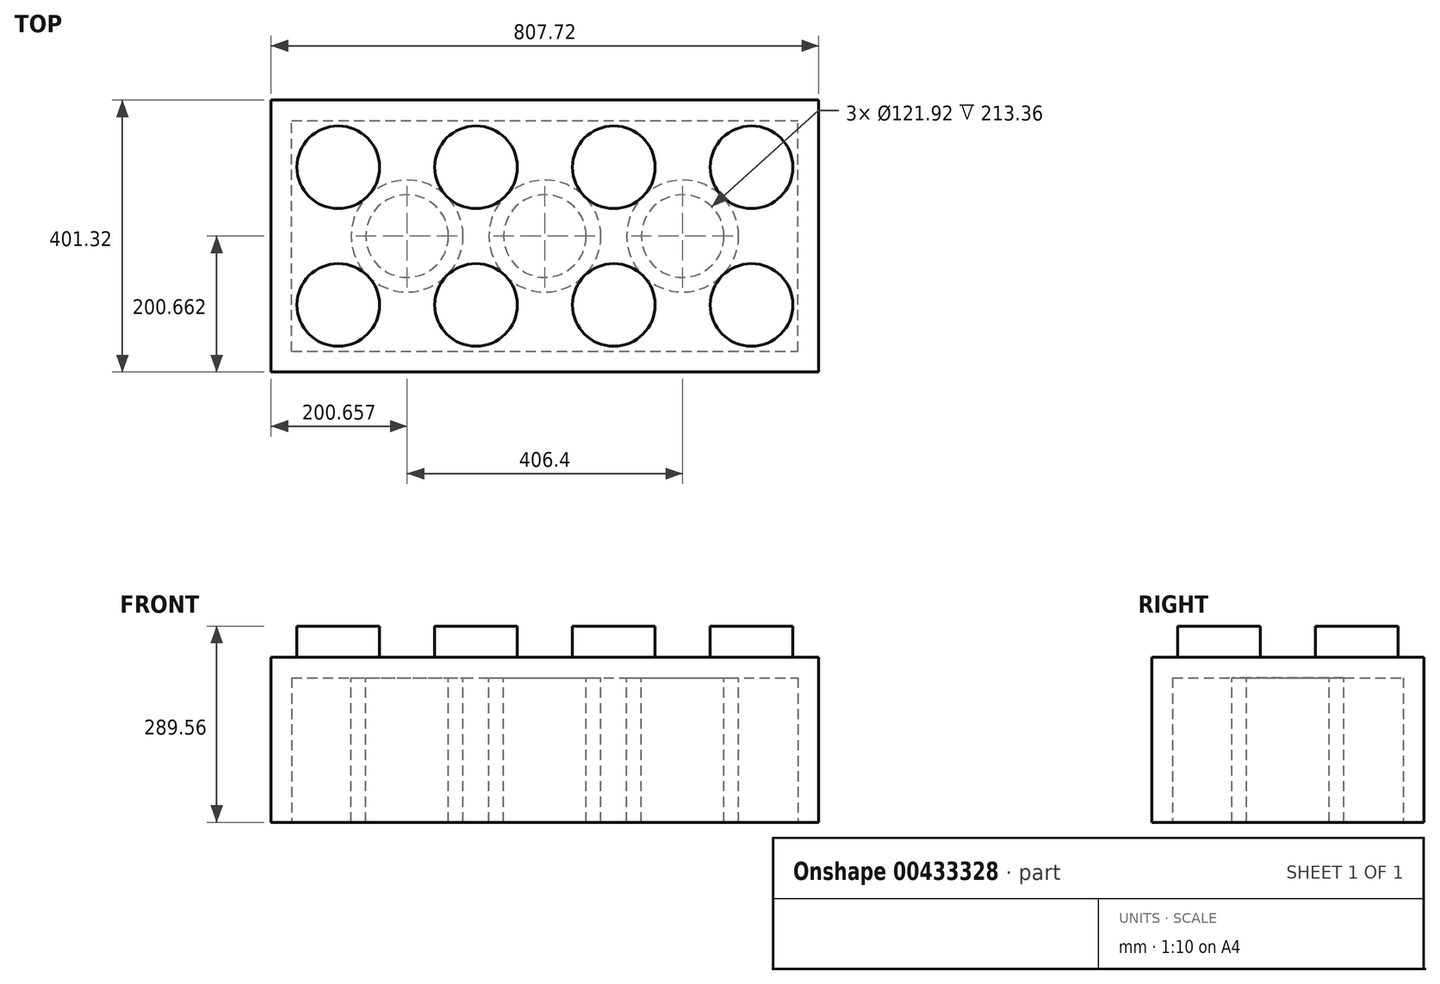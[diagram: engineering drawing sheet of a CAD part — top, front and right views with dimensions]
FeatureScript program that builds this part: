
annotation { "Feature Type Name" : "Feature", "Feature Type Description" : "" }
export const myFeature = defineFeature(function(context is Context, id is Id, definition is map)
    precondition{}
    {
        {
            var Q0;
            Q0=qCreatedBy(makeId("Top.planeOp"),FACE);
            var sketch = newSketch(context, id + "F0", { "sketchPlane" : qUnion([Q0])});
            skLineSegment(sketch, "E0.bottom", {"start": v(-348.7, 195.86) * mm, "end": v(459.02, 195.86) * mm});
            skLineSegment(sketch, "E0.top", {"start": v(-348.7, -205.46) * mm, "end": v(459.02, -205.46) * mm});
            skLineSegment(sketch, "E0.left", {"start": v(-348.7, 195.86) * mm, "end": v(-348.7, -205.46) * mm});
            skLineSegment(sketch, "E0.right", {"start": v(459.02, 195.86) * mm, "end": v(459.02, -205.46) * mm});
            skSolve(sketch);
        }
        {
            var Q0;
            Q0 = qSketchRegion(id + "F0", true);
            extrude(context, id + "F1", {"entities" : qUnion([Q0]), "depth" : 243.84 * mm});
        }
        {
            var Q0;
            Q0=makeQuery(id+"F1.opExtrude","CAP_FACE",FACE,{"disambiguationData":[OSD([sQuery(id+"F0.wireOp",EDGE,"E0.bottom"),sQuery(id+"F0.wireOp",EDGE,"E0.top"),sQuery(id+"F0.wireOp",EDGE,"E0.left"),sQuery(id+"F0.wireOp",EDGE,"E0.right")])],"isStart":false});
            var sketch = newSketch(context, id + "F2", { "sketchPlane" : qUnion([Q0])});
            skCircle(sketch, "E1", {"center": v(-249.64, -106.4) * mm, "radius": 60.96 * mm});
            skCircle(sketch, "E2.0.1.0", {"center": v(-249.64, 96.8) * mm, "radius": 60.96 * mm});
            skCircle(sketch, "E2.1.0.0", {"center": v(-46.44, -106.4) * mm, "radius": 60.96 * mm});
            skCircle(sketch, "E2.1.1.0", {"center": v(-46.44, 96.8) * mm, "radius": 60.96 * mm});
            skCircle(sketch, "E2.2.0.0", {"center": v(156.76, -106.4) * mm, "radius": 60.96 * mm});
            skCircle(sketch, "E2.2.1.0", {"center": v(156.76, 96.8) * mm, "radius": 60.96 * mm});
            skCircle(sketch, "E2.3.0.0", {"center": v(359.96, -106.4) * mm, "radius": 60.96 * mm});
            skCircle(sketch, "E2.3.1.0", {"center": v(359.96, 96.8) * mm, "radius": 60.96 * mm});
            skLineSegment(sketch, "E2.direction1", {"start": v(-249.64, -106.4) * mm, "end": v(-46.44, -106.4) * mm, "construction": true});
            skLineSegment(sketch, "E2.direction2", {"start": v(-249.64, -106.4) * mm, "end": v(-249.64, 96.8) * mm, "construction": true});
            skSolve(sketch);
        }
        {
            var Q0;
            Q0=makeQuery(id+"F2.imprint","IMPRINT",FACE,{"disambiguationData":[TD([[makeQuery(id+"F2.imprint","IMPRINT",EDGE,{"derivedFrom":sQuery(id+"F2.wireOp",EDGE,"E1")}),1.0]])]});
            var Q1;
            Q1=makeQuery(id+"F2.imprint","IMPRINT",FACE,{"disambiguationData":[TD([[makeQuery(id+"F2.imprint","IMPRINT",EDGE,{"derivedFrom":sQuery(id+"F2.wireOp",EDGE,"E2.0.1.0")}),1.0]])]});
            var Q2;
            Q2=makeQuery(id+"F2.imprint","IMPRINT",FACE,{"disambiguationData":[TD([[makeQuery(id+"F2.imprint","IMPRINT",EDGE,{"derivedFrom":sQuery(id+"F2.wireOp",EDGE,"E2.1.0.0")}),1.0]])]});
            var Q3;
            Q3=makeQuery(id+"F2.imprint","IMPRINT",FACE,{"disambiguationData":[TD([[makeQuery(id+"F2.imprint","IMPRINT",EDGE,{"derivedFrom":sQuery(id+"F2.wireOp",EDGE,"E2.1.1.0")}),1.0]])]});
            var Q4;
            Q4=makeQuery(id+"F2.imprint","IMPRINT",FACE,{"disambiguationData":[TD([[makeQuery(id+"F2.imprint","IMPRINT",EDGE,{"derivedFrom":sQuery(id+"F2.wireOp",EDGE,"E2.2.1.0")}),1.0]])]});
            var Q5;
            Q5=makeQuery(id+"F2.imprint","IMPRINT",FACE,{"disambiguationData":[TD([[makeQuery(id+"F2.imprint","IMPRINT",EDGE,{"derivedFrom":sQuery(id+"F2.wireOp",EDGE,"E2.3.0.0")}),1.0]])]});
            var Q6;
            Q6=makeQuery(id+"F2.imprint","IMPRINT",FACE,{"disambiguationData":[TD([[makeQuery(id+"F2.imprint","IMPRINT",EDGE,{"derivedFrom":sQuery(id+"F2.wireOp",EDGE,"E2.3.1.0")}),1.0]])]});
            var Q7;
            Q7=makeQuery(id+"F2.imprint","IMPRINT",FACE,{"disambiguationData":[TD([[makeQuery(id+"F2.imprint","IMPRINT",EDGE,{"derivedFrom":sQuery(id+"F2.wireOp",EDGE,"E2.2.0.0")}),1.0]])]});
            extrude(context, id + "F3", {"entities" : qUnion([Q0, Q1, Q2, Q3, Q4, Q5, Q6, Q7]), "operationType" : NewBodyOperationType.ADD, "depth" : 45.72 * mm});
        }
        {
            var Q0;
            Q0=makeQuery(id+"F1.opExtrude","CAP_FACE",FACE,{"disambiguationData":[OSD([sQuery(id+"F0.wireOp",EDGE,"E0.bottom"),sQuery(id+"F0.wireOp",EDGE,"E0.top"),sQuery(id+"F0.wireOp",EDGE,"E0.left"),sQuery(id+"F0.wireOp",EDGE,"E0.right")])],"isStart":true});
            var sketch = newSketch(context, id + "F4", { "sketchPlane" : qUnion([Q0])});
            skLineSegment(sketch, "E3.bottom", {"start": v(-318.22, 174.98) * mm, "end": v(428.54, 174.98) * mm});
            skLineSegment(sketch, "E3.top", {"start": v(-318.22, -165.38) * mm, "end": v(428.54, -165.38) * mm});
            skLineSegment(sketch, "E3.left", {"start": v(-318.22, 174.98) * mm, "end": v(-318.22, -165.38) * mm});
            skLineSegment(sketch, "E3.right", {"start": v(428.54, 174.98) * mm, "end": v(428.54, -165.38) * mm});
            skSolve(sketch);
        }
        {
            var Q0;
            Q0=makeQuery(id+"F4.imprint","IMPRINT",FACE,{"disambiguationData":[TD([[makeQuery(id+"F4.imprint","IMPRINT",EDGE,{"derivedFrom":sQuery(id+"F4.wireOp",EDGE,"E3.bottom")}),-1.0]])]});
            extrude(context, id + "F5", {"entities" : qUnion([Q0]), "operationType" : NewBodyOperationType.REMOVE, "oppositeDirection" : true, "depth" : 213.36 * mm});
        }
        {
            var Q0;
            Q0=makeQuery(id+"F5.boolean.opBoolean","COPY",FACE,{"derivedFrom":makeQuery(id+"F5.opExtrude","CAP_FACE",FACE,{"disambiguationData":[OSD([sQuery(id+"F4.wireOp",EDGE,"E3.bottom"),sQuery(id+"F4.wireOp",EDGE,"E3.top"),sQuery(id+"F4.wireOp",EDGE,"E3.left"),sQuery(id+"F4.wireOp",EDGE,"E3.right")])],"isStart":false})});
            var sketch = newSketch(context, id + "F6", { "sketchPlane" : qUnion([Q0])});
            skCircle(sketch, "E4", {"center": v(-148.04, 4.8) * mm, "radius": 82.55 * mm});
            skCircle(sketch, "E5", {"center": v(-148.04, 4.8) * mm, "radius": 60.96 * mm});
            skCircle(sketch, "E6.1.0.0", {"center": v(55.16, 4.8) * mm, "radius": 82.55 * mm});
            skCircle(sketch, "E6.1.0.1", {"center": v(55.16, 4.8) * mm, "radius": 60.96 * mm});
            skCircle(sketch, "E6.2.0.0", {"center": v(258.36, 4.8) * mm, "radius": 82.55 * mm});
            skCircle(sketch, "E6.2.0.1", {"center": v(258.36, 4.8) * mm, "radius": 60.96 * mm});
            skLineSegment(sketch, "E6.direction1", {"start": v(-148.04, 4.8) * mm, "end": v(55.16, 4.8) * mm, "construction": true});
            skSolve(sketch);
        }
        {
            var Q0;
            Q0=makeQuery(id+"F6.imprint","IMPRINT",FACE,{"disambiguationData":[TD([[makeQuery(id+"F6.imprint","IMPRINT",EDGE,{"derivedFrom":sQuery(id+"F6.wireOp",EDGE,"E6.1.0.0")}),1.0]])]});
            var Q1;
            Q1=makeQuery(id+"F6.imprint","IMPRINT",FACE,{"disambiguationData":[TD([[makeQuery(id+"F6.imprint","IMPRINT",EDGE,{"derivedFrom":sQuery(id+"F6.wireOp",EDGE,"E6.2.0.0")}),1.0]])]});
            var Q2;
            Q2=makeQuery(id+"F6.imprint","IMPRINT",FACE,{"disambiguationData":[TD([[makeQuery(id+"F6.imprint","IMPRINT",EDGE,{"derivedFrom":sQuery(id+"F6.wireOp",EDGE,"E4")}),1.0]])]});
            extrude(context, id + "F7", {"entities" : qUnion([Q0, Q1, Q2]), "operationType" : NewBodyOperationType.ADD, "depth" : 213.36 * mm});
        }
    });
